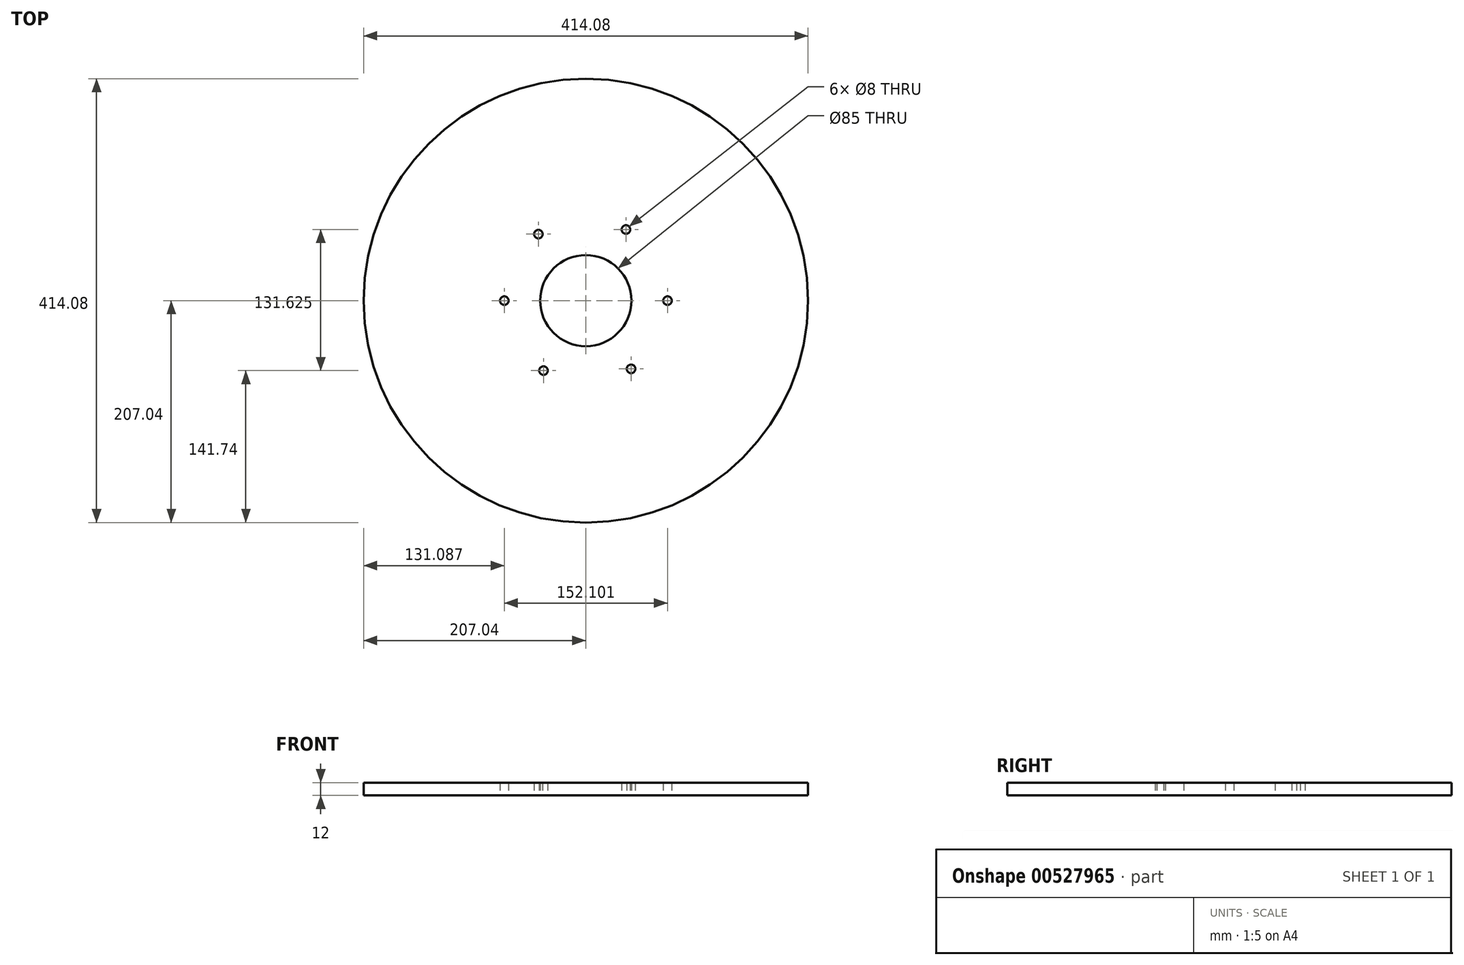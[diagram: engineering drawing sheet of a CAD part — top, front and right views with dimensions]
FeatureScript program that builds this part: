
annotation { "Feature Type Name" : "Feature", "Feature Type Description" : "" }
export const myFeature = defineFeature(function(context is Context, id is Id, definition is map)
    precondition{}
    {
        {
            var Q0;
            Q0=qCreatedBy(makeId("Top.planeOp"),FACE);
            var sketch = newSketch(context, id + "F0", { "sketchPlane" : qUnion([Q0])});
            skCircle(sketch, "E0", {"center": v(0, 0) * mm, "radius": 207.04 * mm});
            skSolve(sketch);
        }
        {
            var Q0;
            Q0=makeQuery(id+"F0.imprint","IMPRINT",FACE,{"disambiguationData":[TD([[makeQuery(id+"F0.imprint","IMPRINT",EDGE,{"derivedFrom":sQuery(id+"F0.wireOp",EDGE,"E0")}),1.0]])]});
            var Q1;
            Q1=sQuery(id+"F0.wireOp",EDGE,"E0");
            extrude(context, id + "F1", {"entities" : qUnion([Q0]), "surfaceEntities" : qUnion([Q1]), "depth" : 12 * mm, "offsetDistance" : 25 * mm});
        }
        {
            var Q0;
            Q0=makeQuery(id+"F1.opExtrude","CAP_FACE",FACE,{"disambiguationData":[OSD([sQuery(id+"F0.wireOp",EDGE,"E0")])],"isStart":true});
            var sketch = newSketch(context, id + "F2", { "sketchPlane" : qUnion([Q0])});
            skPoint(sketch, "E1", {"position": v(0, 0) * mm});
            skSolve(sketch);
        }
        {
            var Q0;
            Q0=sQuery(id+"F2.wireOp",VERTEX,"E1");
            var Q1;
            Q1=makeQuery(id+"F1.opExtrude","SWEPT_BODY",BODY,{"disambiguationData":[OSD([sQuery(id+"F0.wireOp",EDGE,"E0")])]});
            hole(context, id + "F3", {"style" : HoleStyle.SIMPLE, "endStyle" : HoleEndStyle.THROUGH, "holeDiameter" : 85 * mm, "isTappedThrough" : true, "tappedDepth" : 12 * mm, "tapClearance" : 3, "locations" : qUnion([Q0]), "scope" : qUnion([Q1])});
        }
        {
            var Q0;
            Q0=makeQuery(id+"F1.opExtrude","CAP_FACE",FACE,{"disambiguationData":[OSD([sQuery(id+"F0.wireOp",EDGE,"E0")])],"isStart":true});
            var sketch = newSketch(context, id + "F4", { "sketchPlane" : qUnion([Q0])});
            skCircle(sketch, "E2", {"center": v(0, 0) * mm, "radius": 76.26 * mm});
            skSolve(sketch);
        }
        {
            var Q0;
            Q0=makeQuery(id+"F4.imprint","IMPRINT",FACE,{"disambiguationData":[TD([[makeQuery(id+"F4.imprint","IMPRINT",EDGE,{"derivedFrom":sQuery(id+"F4.wireOp",EDGE,"E2")}),-1.0]])]});
            var sketch = newSketch(context, id + "F5", { "sketchPlane" : qUnion([Q0])});
            skPoint(sketch, "E3", {"position": v(76.15, 0) * mm});
            skPoint(sketch, "E4", {"position": v(37.44, -66.32) * mm});
            skPoint(sketch, "E5", {"position": v(-44.15, -62) * mm});
            skPoint(sketch, "E6", {"position": v(-75.95, 0) * mm});
            skPoint(sketch, "E7", {"position": v(-39.41, 65.3) * mm});
            skPoint(sketch, "E8", {"position": v(42.2, 63.68) * mm});
            skSolve(sketch);
        }
        {
            var Q0;
            Q0=sQuery(id+"F5.wireOp",VERTEX,"E6");
            var Q1;
            Q1=sQuery(id+"F5.wireOp",VERTEX,"E7");
            var Q2;
            Q2=sQuery(id+"F5.wireOp",VERTEX,"E8");
            var Q3;
            Q3=sQuery(id+"F5.wireOp",VERTEX,"E3");
            var Q4;
            Q4=sQuery(id+"F5.wireOp",VERTEX,"E4");
            var Q5;
            Q5=sQuery(id+"F5.wireOp",VERTEX,"E5");
            var Q6;
            Q6=makeQuery(id+"F1.opExtrude","SWEPT_BODY",BODY,{"disambiguationData":[OSD([sQuery(id+"F0.wireOp",EDGE,"E0")])]});
            hole(context, id + "F6", {"style" : HoleStyle.SIMPLE, "endStyle" : HoleEndStyle.THROUGH, "holeDiameter" : 8 * mm, "isTappedThrough" : true, "tappedDepth" : 12 * mm, "tapClearance" : 3, "locations" : qUnion([Q0, Q1, Q2, Q3, Q4, Q5]), "scope" : qUnion([Q6])});
        }
    });
